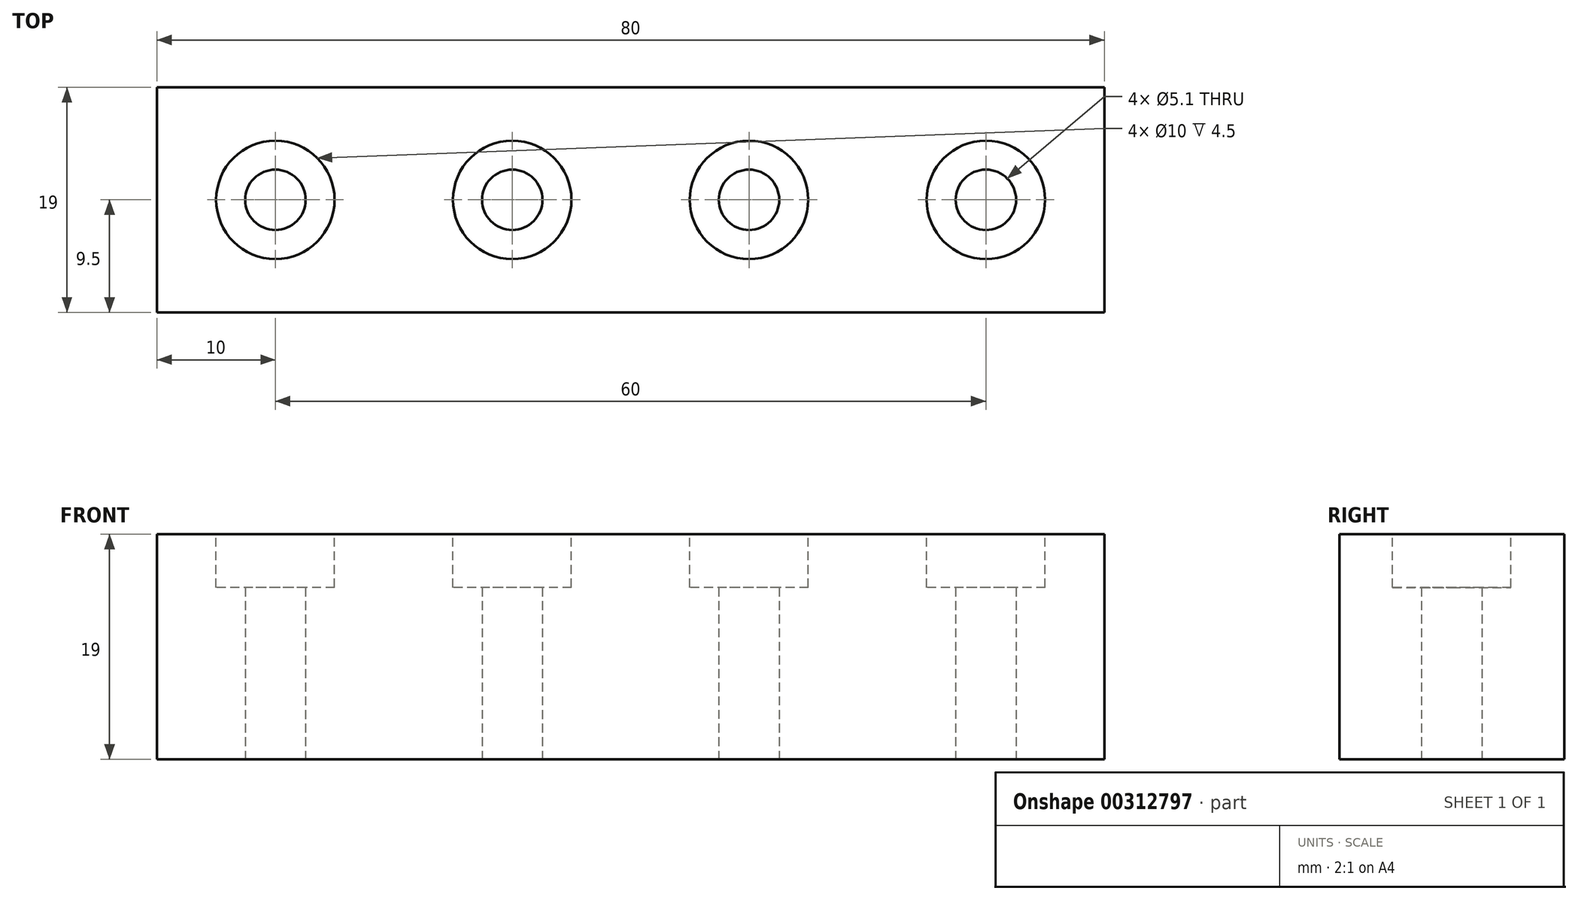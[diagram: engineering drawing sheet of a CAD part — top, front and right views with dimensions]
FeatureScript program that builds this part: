
annotation { "Feature Type Name" : "Feature", "Feature Type Description" : "" }
export const myFeature = defineFeature(function(context is Context, id is Id, definition is map)
    precondition{}
    {
        {
            var Q0;
            Q0=qCreatedBy(makeId("Top.planeOp"),FACE);
            var sketch = newSketch(context, id + "F0", { "sketchPlane" : qUnion([Q0])});
            skLineSegment(sketch, "E0.bottom", {"start": v(40, -9.5) * mm, "end": v(-40, -9.5) * mm});
            skLineSegment(sketch, "E0.top", {"start": v(40, 9.5) * mm, "end": v(-40, 9.5) * mm});
            skLineSegment(sketch, "E0.left", {"start": v(40, -9.5) * mm, "end": v(40, 9.5) * mm});
            skLineSegment(sketch, "E0.right", {"start": v(-40, -9.5) * mm, "end": v(-40, 9.5) * mm});
            skPoint(sketch, "E0.middle", {"position": v(0, 0) * mm});
            skLineSegment(sketch, "E1", {"start": v(-40, 0) * mm, "end": v(40, 0) * mm, "construction": true});
            skCircle(sketch, "E2", {"center": v(-30, 0) * mm, "radius": 2.55 * mm});
            skCircle(sketch, "E3", {"center": v(-10, 0) * mm, "radius": 2.55 * mm});
            skCircle(sketch, "E4", {"center": v(10, 0) * mm, "radius": 2.55 * mm});
            skCircle(sketch, "E5", {"center": v(30, 0) * mm, "radius": 2.55 * mm});
            skSolve(sketch);
        }
        {
            var Q0;
            Q0=makeQuery(id+"F0.imprint","IMPRINT",FACE,{"disambiguationData":[TD([[makeQuery(id+"F0.imprint","IMPRINT",EDGE,{"derivedFrom":sQuery(id+"F0.wireOp",EDGE,"E0.bottom")}),-1.0]])]});
            extrude(context, id + "F1", {"entities" : qUnion([Q0]), "depth" : 19 * mm});
        }
        {
            var Q0;
            Q0=makeQuery(id+"F1.opExtrude","CAP_FACE",FACE,{"disambiguationData":[OSD([sQuery(id+"F0.wireOp",EDGE,"E0.bottom"),sQuery(id+"F0.wireOp",EDGE,"E0.top"),sQuery(id+"F0.wireOp",EDGE,"E0.left"),sQuery(id+"F0.wireOp",EDGE,"E0.right"),sQuery(id+"F0.wireOp",EDGE,"E2"),sQuery(id+"F0.wireOp",EDGE,"E3"),sQuery(id+"F0.wireOp",EDGE,"E4"),sQuery(id+"F0.wireOp",EDGE,"E5")])],"isStart":false});
            var sketch = newSketch(context, id + "F2", { "sketchPlane" : qUnion([Q0])});
            skCircle(sketch, "E6", {"center": v(-30, 0) * mm, "radius": 5 * mm});
            skCircle(sketch, "E7", {"center": v(-10, 0) * mm, "radius": 5 * mm});
            skCircle(sketch, "E8", {"center": v(10, 0) * mm, "radius": 5 * mm});
            skCircle(sketch, "E9", {"center": v(30, 0) * mm, "radius": 5 * mm});
            skSolve(sketch);
        }
        {
            var Q0;
            Q0=qSketchRegion(id+"F2",true);
            extrude(context, id + "F3", {"entities" : qUnion([Q0]), "operationType" : NewBodyOperationType.REMOVE, "oppositeDirection" : true, "depth" : 4.5 * mm});
        }
    });
